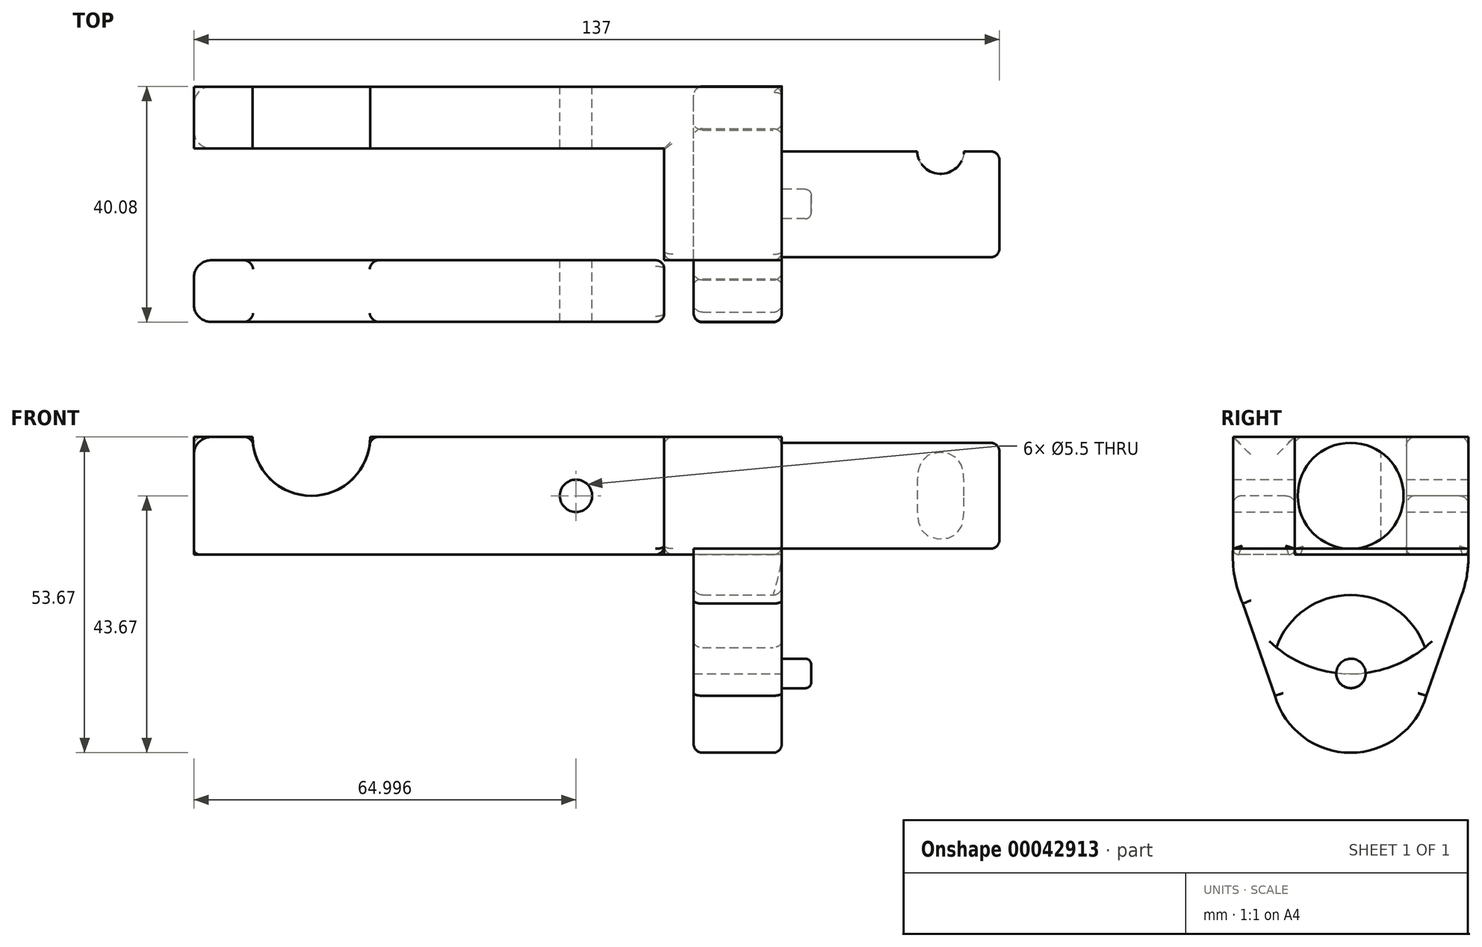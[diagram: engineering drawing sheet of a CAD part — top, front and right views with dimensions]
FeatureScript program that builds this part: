
annotation { "Feature Type Name" : "Feature", "Feature Type Description" : "" }
export const myFeature = defineFeature(function(context is Context, id is Id, definition is map)
    precondition{}
    {
        {
            var Q0;
            Q0=qCreatedBy(makeId("Top.planeOp"),FACE);
            var sketch = newSketch(context, id + "F0", { "sketchPlane" : qUnion([Q0])});
            skLineSegment(sketch, "E0.bottom", {"start": v(-43.64, 0) * mm, "end": v(37.87, 0) * mm});
            skLineSegment(sketch, "E0.top", {"start": v(-43.64, -10.5) * mm, "end": v(37.87, -10.5) * mm});
            skLineSegment(sketch, "E0.left", {"start": v(-43.64, 0) * mm, "end": v(-43.64, -10.5) * mm});
            skLineSegment(sketch, "E0.right", {"start": v(37.87, 0) * mm, "end": v(37.87, -10.5) * mm});
            skLineSegment(sketch, "E1.bottom", {"start": v(36.36, 0) * mm, "end": v(56.36, 0) * mm});
            skLineSegment(sketch, "E1.top", {"start": v(36.36, -40) * mm, "end": v(56.36, -40) * mm});
            skLineSegment(sketch, "E1.left", {"start": v(36.36, 0) * mm, "end": v(36.36, -40) * mm});
            skLineSegment(sketch, "E1.right", {"start": v(56.36, 0) * mm, "end": v(56.36, -40) * mm});
            skPoint(sketch, "E2.oppositeSnap0", {"position": v(46.36, -40) * mm});
            skLineSegment(sketch, "E2.bottom", {"start": v(56.36, -29.5) * mm, "end": v(-43.64, -29.5) * mm});
            skLineSegment(sketch, "E2.top", {"start": v(56.36, -40) * mm, "end": v(-43.64, -40) * mm});
            skLineSegment(sketch, "E2.left", {"start": v(56.36, -29.5) * mm, "end": v(56.36, -40) * mm});
            skLineSegment(sketch, "E2.right", {"start": v(-43.64, -29.5) * mm, "end": v(-43.64, -40) * mm});
            skSolve(sketch);
        }
        {
            var Q0;
            {var subQ3=sQuery(id+"F0.wireOp",EDGE,"E0.bottom");Q0=makeQuery(id+"F0.imprint","IMPRINT",FACE,{"disambiguationData":[TD([[makeQuery(id+"F0.imprint","IMPRINT",EDGE,{"derivedFrom":subQ3}),-1.0]])]});}
            var Q1;
            {var subQ6=sQuery(id+"F0.wireOp",EDGE,"E0.right");Q1=makeQuery(id+"F0.imprint","IMPRINT",FACE,{"disambiguationData":[TD([[makeQuery(id+"F0.imprint","IMPRINT",EDGE,{"derivedFrom":subQ6}),1.0]])]});}
            var Q2;
            {var subQ5=sQuery(id+"F0.wireOp",EDGE,"E0.right");Q2=makeQuery(id+"F0.imprint","IMPRINT",FACE,{"disambiguationData":[TD([[makeQuery(id+"F0.imprint","IMPRINT",EDGE,{"derivedFrom":subQ5}),-1.0]])]});}
            var Q3;
            {var subQ0=sQuery(id+"F0.wireOp",EDGE,"E2.right");Q3=makeQuery(id+"F0.imprint","IMPRINT",FACE,{"disambiguationData":[TD([[makeQuery(id+"F0.imprint","IMPRINT",EDGE,{"derivedFrom":subQ0}),1.0]])]});}
            var Q4;
            {var subQ0=sQuery(id+"F0.wireOp",EDGE,"E2.left");Q4=makeQuery(id+"F0.imprint","IMPRINT",FACE,{"disambiguationData":[TD([[makeQuery(id+"F0.imprint","IMPRINT",EDGE,{"derivedFrom":subQ0}),-1.0]])]});}
            extrude(context, id + "F1", {"entities" : qUnion([Q0, Q1, Q2, Q3, Q4]), "depth" : 20 * mm});
        }
        {
            var Q0;
            Q0=makeQuery(id+"F1.opExtrude","SWEPT_FACE",FACE,{"disambiguationData":[OSD([sQuery(id+"F0.wireOp",EDGE,"E2.top")])]});
            var sketch = newSketch(context, id + "F2", { "sketchPlane" : qUnion([Q0])});
            skArc(sketch, "E3", {"start": v(-33.64, 20) * mm, "mid": v(-23.64, 10) * mm, "end": v(-13.64, 20) * mm});
            skSolve(sketch);
        }
        {
            var Q0;
            {var subQ1=sQuery(id+"F2.wireOp",EDGE,"E3");Q0=makeQuery(id+"F2.imprint","IMPRINT",FACE,{"disambiguationData":[TD([[makeQuery(id+"F2.imprint","IMPRINT",EDGE,{"derivedFrom":subQ1}),1.0]])]});}
            extrude(context, id + "F3", {"entities" : qUnion([Q0]), "operationType" : NewBodyOperationType.REMOVE, "oppositeDirection" : true, "depth" : 52.24 * mm});
        }
        {
            var Q0;
            Q0=makeQuery(id+"F1.opExtrude","SWEPT_FACE",FACE,{"disambiguationData":[OSD([sQuery(id+"F0.wireOp",EDGE,"E0.bottom"),sQuery(id+"F0.wireOp",EDGE,"E1.bottom")])]});
            var sketch = newSketch(context, id + "F4", { "sketchPlane" : qUnion([Q0])});
            skCircle(sketch, "E4", {"center": v(-21.36, 10) * mm, "radius": 2.75 * mm});
            skSolve(sketch);
        }
        {
            var Q0;
            Q0=makeQuery(id+"F1.opExtrude","SWEPT_FACE",FACE,{"disambiguationData":[OSD([sQuery(id+"F0.wireOp",EDGE,"E1.right"),sQuery(id+"F0.wireOp",EDGE,"E2.left")])]});
            var sketch = newSketch(context, id + "F5", { "sketchPlane" : qUnion([Q0])});
            skCircle(sketch, "E5", {"center": v(-20, 10) * mm, "radius": 9 * mm});
            skPoint(sketch, "E5.centerSnap0", {"position": v(-20, 19) * mm});
            skPoint(sketch, "E5.centerSnap1", {"position": v(-40, 10) * mm});
            skSolve(sketch);
        }
        {
            var Q0;
            Q0=makeQuery(id+"F4.imprint","IMPRINT",FACE,{"disambiguationData":[TD([[makeQuery(id+"F4.imprint","IMPRINT",EDGE,{"derivedFrom":sQuery(id+"F4.wireOp",EDGE,"E4")}),1.0]])]});
            extrude(context, id + "F6", {"entities" : qUnion([Q0]), "operationType" : NewBodyOperationType.REMOVE, "oppositeDirection" : true, "depth" : 50.64 * mm});
        }
        {
            var Q0;
            {var subQ0=sQuery(id+"F0.wireOp",EDGE,"E1.right");var subQ1=sQuery(id+"F0.wireOp",EDGE,"E2.left");var subQ2=makeQuery(id+"F1.opExtrude","SWEPT_FACE",FACE,{"disambiguationData":[OSD([subQ0,subQ1])]});var subQ3=sQuery(id+"F0.wireOp",EDGE,"E0.bottom");var subQ4=sQuery(id+"F0.wireOp",EDGE,"E1.bottom");var subQ5=makeQuery(id+"F1.opExtrude","SWEPT_FACE",FACE,{"disambiguationData":[OSD([subQ3,subQ4])]});Q0=makeQuery(id+"FOvGjot31i7O7Zv_1.boolean.opBoolean","SPLIT",FACE,{"disambiguationData":[TD([subQ5])],"derivedFrom":subQ2});}
            var sketch = newSketch(context, id + "F7", { "sketchPlane" : qUnion([Q0])});
            skArc(sketch, "E6", {"start": v(-40, 1) * mm, "mid": v(-20, -20.26) * mm, "end": v(0, 1) * mm});
            skLineSegment(sketch, "E7", {"start": v(-40, 1) * mm, "end": v(0, 1) * mm});
            skCircle(sketch, "E8", {"center": v(-20, -20.26) * mm, "radius": 13.4 * mm});
            skLineSegment(sketch, "E9", {"start": v(-32.88, -23.99) * mm, "end": v(-39.4, -5.25) * mm});
            skLineSegment(sketch, "E10", {"start": v(-7.12, -23.99) * mm, "end": v(-0.52, -5.25) * mm});
            skSolve(sketch);
        }
        {
            var Q0;
            Q0 = qSketchRegion(id + "F7", true);
            var Q1;
            {var subQ0=sQuery(id+"F7.wireOp",EDGE,"E8");var subQ1=sQuery(id+"F7.wireOp",EDGE,"E6");var subQ3=makeQuery(id+"F7.imprint","INTERSECT",VERTEX,{"disambiguationData":[OD(0.0)],"derivedFrom":[subQ1,subQ0]});Q1=makeQuery(id+"F7.imprint","IMPRINT",FACE,{"disambiguationData":[TD([[makeQuery(id+"F7.imprint","IMPRINT",EDGE,{"disambiguationData":[TD([[subQ3,-1.0]])],"derivedFrom":subQ1}),1.0]])]});}
            extrude(context, id + "F8", {"entities" : qUnion([Q0, Q1]), "oppositeDirection" : true, "depth" : 15 * mm});
        }
        {
            var Q0;
            Q0=makeQuery(id+"F1.opExtrude","SWEPT_BODY",BODY,{"disambiguationData":[OSD([sQuery(id+"F0.wireOp",EDGE,"E0.bottom"),sQuery(id+"F0.wireOp",EDGE,"E0.top"),sQuery(id+"F0.wireOp",EDGE,"E0.left"),sQuery(id+"F0.wireOp",EDGE,"E1.bottom"),sQuery(id+"F0.wireOp",EDGE,"E1.left"),sQuery(id+"F0.wireOp",EDGE,"E1.right"),sQuery(id+"F0.wireOp",EDGE,"E2.bottom"),sQuery(id+"F0.wireOp",EDGE,"E2.top"),sQuery(id+"F0.wireOp",EDGE,"E2.left"),sQuery(id+"F0.wireOp",EDGE,"E2.right")])]});
            transform(context, id + "F9", {"entities" : qUnion([Q0]), "transformType" : TransformType.TRANSLATION_3D, "dx" : 0 * mm, "dy" : 0 * mm, "dz" : 0 * mm, "makeCopy" : true});
        }
        {
            var Q0;
            Q0 = qSketchRegion(id + "F5", true);
            extrude(context, id + "F10", {"entities" : qUnion([Q0]), "depth" : 37 * mm});
        }
        {
            var Q0;
            {var subQ0=sQuery(id+"F0.wireOp",EDGE,"E0.bottom");var subQ1=sQuery(id+"F0.wireOp",EDGE,"E0.top");var subQ2=sQuery(id+"F0.wireOp",EDGE,"E1.bottom");var subQ3=sQuery(id+"F0.wireOp",EDGE,"E1.left");var subQ4=sQuery(id+"F0.wireOp",EDGE,"E1.right");var subQ5=sQuery(id+"F0.wireOp",EDGE,"E2.bottom");var subQ6=sQuery(id+"F0.wireOp",EDGE,"E2.top");var subQ7=sQuery(id+"F0.wireOp",EDGE,"E2.left");Q0=makeQuery(id+"F3.boolean.opBoolean","SPLIT",FACE,{"disambiguationData":[TD([makeQuery(id+"F1.opExtrude","SWEPT_FACE",FACE,{"disambiguationData":[OSD([subQ3])]})])],"derivedFrom":makeQuery(id+"F1.opExtrude","CAP_FACE",FACE,{"disambiguationData":[OSD([subQ0,subQ1,sQuery(id+"F0.wireOp",EDGE,"E0.left"),subQ2,subQ3,subQ4,subQ5,subQ6,subQ7,sQuery(id+"F0.wireOp",EDGE,"E2.right")])],"isStart":false})});}
            var sketch = newSketch(context, id + "F11", { "sketchPlane" : qUnion([Q0])});
            skArc(sketch, "E11", {"start": v(79.36, -29.28) * mm, "mid": v(83.34, -25.17) * mm, "end": v(87.35, -29.25) * mm});
            skLineSegment(sketch, "E12", {"start": v(79.36, -29.28) * mm, "end": v(87.35, -29.25) * mm});
            skArc(sketch, "E13", {"start": v(79.36, -10.7) * mm, "mid": v(83.3, -14.8) * mm, "end": v(87.35, -10.8) * mm});
            skLineSegment(sketch, "E14", {"start": v(79.36, -10.7) * mm, "end": v(87.35, -10.8) * mm});
            skSolve(sketch);
        }
        {
            var Q0;
            Q0=makeQuery(id+"F11.imprint","IMPRINT",FACE,{"disambiguationData":[TD([[makeQuery(id+"F11.imprint","IMPRINT",EDGE,{"derivedFrom":sQuery(id+"F11.wireOp",EDGE,"bea93a81-216b-46dd-bc57-cd59c5f029c9")}),1.0]])]});
            var Q1;
            Q1=makeQuery(id+"F11.imprint","IMPRINT",FACE,{"disambiguationData":[TD([[makeQuery(id+"F11.imprint","IMPRINT",EDGE,{"derivedFrom":sQuery(id+"F11.wireOp",EDGE,"bffc142d-1d58-4124-9edf-efa4acdb14e5")}),1.0]])]});
            var Q2;
            Q2=makeQuery(id+"F11.imprint","IMPRINT",FACE,{"disambiguationData":[TD([[makeQuery(id+"F11.imprint","IMPRINT",EDGE,{"derivedFrom":sQuery(id+"F11.wireOp",EDGE,"E11")}),-1.0]])]});
            var Q3;
            Q3=makeQuery(id+"F11.imprint","IMPRINT",FACE,{"disambiguationData":[TD([[makeQuery(id+"F11.imprint","IMPRINT",EDGE,{"derivedFrom":sQuery(id+"F11.wireOp",EDGE,"E13")}),1.0]])]});
            extrude(context, id + "F12", {"entities" : qUnion([Q0, Q1, Q2, Q3]), "operationType" : NewBodyOperationType.REMOVE, "oppositeDirection" : true, "depth" : 25 * mm});
        }
        {
            var Q0;
            {var subQ0=sQuery(id+"F7.wireOp",EDGE,"E8");var subQ1=sQuery(id+"F7.wireOp",EDGE,"E6");var subQ5=makeQuery(id+"F7.imprint","INTERSECT",VERTEX,{"disambiguationData":[OD(0.0)],"derivedFrom":[subQ1,subQ0]});Q0=makeQuery(id+"F7.imprint","IMPRINT",FACE,{"disambiguationData":[TD([[makeQuery(id+"F7.imprint","IMPRINT",EDGE,{"disambiguationData":[TD([[subQ5,-1.0]])],"derivedFrom":subQ1}),-1.0]])]});}
            var sketch = newSketch(context, id + "F13", { "sketchPlane" : qUnion([Q0])});
            skCircle(sketch, "E15", {"center": v(-19.94, -20.2) * mm, "radius": 2.5 * mm});
            skSolve(sketch);
        }
        {
            var Q0;
            {var subQ0=sQuery(id+"F7.wireOp",EDGE,"E6");var subQ1=sQuery(id+"F7.wireOp",EDGE,"E8");var subQ2=makeQuery(id+"F7.imprint","IMPRINT",EDGE,{"disambiguationData":[TD([[makeQuery(id+"F7.imprint","INTERSECT",VERTEX,{"disambiguationData":[OD(0.0)],"derivedFrom":[subQ0,subQ1]}),-1.0]])],"derivedFrom":subQ0});var subQ3=sQuery(id+"F13.wireOp",EDGE,"E15");var subQ5=makeQuery(id+"F13.imprint","INTERSECT",VERTEX,{"disambiguationData":[OD(0.0)],"derivedFrom":[subQ2,subQ3]});Q0=makeQuery(id+"F13.imprint","IMPRINT",FACE,{"disambiguationData":[TD([[makeQuery(id+"F13.imprint","IMPRINT",EDGE,{"disambiguationData":[TD([[subQ5,-1.0]])],"derivedFrom":subQ3}),1.0]])]});}
            var Q1;
            {var subQ0=sQuery(id+"F7.wireOp",EDGE,"E6");var subQ1=sQuery(id+"F7.wireOp",EDGE,"E8");var subQ2=makeQuery(id+"F7.imprint","IMPRINT",EDGE,{"disambiguationData":[TD([[makeQuery(id+"F7.imprint","INTERSECT",VERTEX,{"disambiguationData":[OD(0.0)],"derivedFrom":[subQ0,subQ1]}),-1.0]])],"derivedFrom":subQ0});var subQ3=sQuery(id+"F13.wireOp",EDGE,"E15");var subQ5=makeQuery(id+"F13.imprint","INTERSECT",VERTEX,{"disambiguationData":[OD(0.0)],"derivedFrom":[subQ2,subQ3]});Q1=makeQuery(id+"F13.imprint","IMPRINT",FACE,{"disambiguationData":[TD([[makeQuery(id+"F13.imprint","IMPRINT",EDGE,{"disambiguationData":[TD([[subQ5,1.0]])],"derivedFrom":subQ3}),1.0]])]});}
            extrude(context, id + "F14", {"entities" : qUnion([Q0, Q1]), "operationType" : NewBodyOperationType.ADD, "depth" : 5 * mm});
        }
        {
            var Q0;
            {var subQ0=sQuery(id+"F0.wireOp",EDGE,"E0.bottom");var subQ1=sQuery(id+"F0.wireOp",EDGE,"E0.top");var subQ2=sQuery(id+"F0.wireOp",EDGE,"E1.bottom");var subQ3=sQuery(id+"F0.wireOp",EDGE,"E1.left");var subQ4=sQuery(id+"F0.wireOp",EDGE,"E1.right");var subQ5=sQuery(id+"F0.wireOp",EDGE,"E2.bottom");var subQ6=sQuery(id+"F0.wireOp",EDGE,"E2.top");var subQ7=sQuery(id+"F0.wireOp",EDGE,"E2.left");Q0=makeQuery(id+"F3.boolean.opBoolean","SPLIT",FACE,{"disambiguationData":[TD([makeQuery(id+"F1.opExtrude","SWEPT_FACE",FACE,{"disambiguationData":[OSD([subQ3])]})])],"derivedFrom":makeQuery(id+"F1.opExtrude","CAP_FACE",FACE,{"disambiguationData":[OSD([subQ0,subQ1,sQuery(id+"F0.wireOp",EDGE,"E0.left"),subQ2,subQ3,subQ4,subQ5,subQ6,subQ7,sQuery(id+"F0.wireOp",EDGE,"E2.right")])],"isStart":false})});}
            var Q1;
            {var subQ0=sQuery(id+"F0.wireOp",EDGE,"E0.bottom");var subQ1=sQuery(id+"F0.wireOp",EDGE,"E0.top");var subQ2=sQuery(id+"F0.wireOp",EDGE,"E0.left");var subQ3=sQuery(id+"F0.wireOp",EDGE,"E1.bottom");Q1=makeQuery(id+"F3.boolean.opBoolean","SPLIT",FACE,{"disambiguationData":[TD([makeQuery(id+"F1.opExtrude","SWEPT_FACE",FACE,{"disambiguationData":[OSD([subQ2])]})])],"derivedFrom":makeQuery(id+"F1.opExtrude","CAP_FACE",FACE,{"disambiguationData":[OSD([subQ0,subQ1,subQ2,subQ3,sQuery(id+"F0.wireOp",EDGE,"E1.left"),sQuery(id+"F0.wireOp",EDGE,"E1.right"),sQuery(id+"F0.wireOp",EDGE,"E2.bottom"),sQuery(id+"F0.wireOp",EDGE,"E2.top"),sQuery(id+"F0.wireOp",EDGE,"E2.left"),sQuery(id+"F0.wireOp",EDGE,"E2.right")])],"isStart":false})});}
            var Q2;
            {var subQ0=sQuery(id+"F0.wireOp",EDGE,"E2.bottom");var subQ1=sQuery(id+"F0.wireOp",EDGE,"E2.top");var subQ2=sQuery(id+"F0.wireOp",EDGE,"E2.right");Q2=makeQuery(id+"F3.boolean.opBoolean","SPLIT",FACE,{"disambiguationData":[TD([makeQuery(id+"F1.opExtrude","SWEPT_FACE",FACE,{"disambiguationData":[OSD([subQ2])]})])],"derivedFrom":makeQuery(id+"F1.opExtrude","CAP_FACE",FACE,{"disambiguationData":[OSD([sQuery(id+"F0.wireOp",EDGE,"E0.bottom"),sQuery(id+"F0.wireOp",EDGE,"E0.top"),sQuery(id+"F0.wireOp",EDGE,"E0.left"),sQuery(id+"F0.wireOp",EDGE,"E1.bottom"),sQuery(id+"F0.wireOp",EDGE,"E1.left"),sQuery(id+"F0.wireOp",EDGE,"E1.right"),subQ0,subQ1,sQuery(id+"F0.wireOp",EDGE,"E2.left"),subQ2])],"isStart":false})});}
            var Q3;
            Q3=makeQuery(id+"F3.boolean.opBoolean","COPY",FACE,{"disambiguationData":[OD(0.0)],"derivedFrom":makeQuery(id+"F3.opExtrude","SWEPT_FACE",FACE,{"disambiguationData":[OSD([sQuery(id+"F2.wireOp",EDGE,"E3")])]})});
            var Q4;
            Q4=makeQuery(id+"F3.boolean.opBoolean","COPY",FACE,{"disambiguationData":[OD(1.0)],"derivedFrom":makeQuery(id+"F3.opExtrude","SWEPT_FACE",FACE,{"disambiguationData":[OSD([sQuery(id+"F2.wireOp",EDGE,"E3")])]})});
            fillet(context, id + "F15", {"entities" : qUnion([Q0, Q1, Q2, Q3, Q4]), "radius" : 1.5 * mm, "tangentPropagation" : true, "allowEdgeOverflow" : false});
        }
        {
            var Q0;
            Q0=makeQuery(id+"F1.opExtrude","CAP_EDGE",EDGE,{"disambiguationData":[OSD([sQuery(id+"F0.wireOp",EDGE,"E2.right")])],"isStart":true});
            var Q1;
            Q1=makeQuery(id+"F1.opExtrude","CAP_EDGE",EDGE,{"disambiguationData":[OSD([sQuery(id+"F0.wireOp",EDGE,"E2.bottom")])],"isStart":true});
            var Q2;
            Q2=makeQuery(id+"F1.opExtrude","CAP_EDGE",EDGE,{"disambiguationData":[OSD([sQuery(id+"F0.wireOp",EDGE,"E2.top")])],"isStart":true});
            var Q3;
            Q3=makeQuery(id+"F1.opExtrude","CAP_EDGE",EDGE,{"disambiguationData":[OSD([sQuery(id+"F0.wireOp",EDGE,"E0.top")])],"isStart":true});
            var Q4;
            Q4=makeQuery(id+"F1.opExtrude","CAP_EDGE",EDGE,{"disambiguationData":[OSD([sQuery(id+"F0.wireOp",EDGE,"E0.left")])],"isStart":true});
            var Q5;
            Q5=makeQuery(id+"F1.opExtrude","CAP_EDGE",EDGE,{"disambiguationData":[OSD([sQuery(id+"F0.wireOp",EDGE,"E0.bottom"),sQuery(id+"F0.wireOp",EDGE,"E1.bottom")])],"isStart":true});
            fillet(context, id + "F16", {"entities" : qUnion([Q0, Q1, Q2, Q3, Q4, Q5]), "radius" : 1 * mm, "tangentPropagation" : true, "allowEdgeOverflow" : false});
        }
        {
            var Q0;
            {var subQ0=sQuery(id+"F7.wireOp",EDGE,"E6");var subQ1=sQuery(id+"F7.wireOp",EDGE,"E9");var subQ2=makeQuery(id+"F7.imprint","INTERSECT",VERTEX,{"disambiguationData":[OD(0.0)],"derivedFrom":[subQ0,subQ1]});Q0=makeQuery(id+"F8.opExtrude","CAP_EDGE",EDGE,{"disambiguationData":[OSD([subQ0]),TDD([makeQuery(id+"F7.imprint","IMPRINT",EDGE,{"disambiguationData":[TD([[subQ2,1.0]])],"derivedFrom":subQ0}),makeQuery(id+"F7.imprint","IMPRINT",EDGE,{"disambiguationData":[TD([[subQ2,-1.0]])],"derivedFrom":subQ0})])],"isStart":false});}
            var Q1;
            Q1=makeQuery(id+"F8.opExtrude","CAP_EDGE",EDGE,{"disambiguationData":[OSD([sQuery(id+"F7.wireOp",EDGE,"E10")])],"isStart":false});
            var Q2;
            Q2=makeQuery(id+"F8.opExtrude","CAP_EDGE",EDGE,{"disambiguationData":[OSD([sQuery(id+"F7.wireOp",EDGE,"E8")])],"isStart":false});
            fillet(context, id + "F17", {"entities" : qUnion([Q0, Q1, Q2]), "radius" : 1.5 * mm, "tangentPropagation" : true, "allowEdgeOverflow" : false});
        }
        {
            var Q0;
            Q0=makeQuery(id+"F8.opExtrude","CAP_EDGE",EDGE,{"disambiguationData":[OSD([sQuery(id+"F7.wireOp",EDGE,"E8")])],"isStart":true});
            var Q1;
            {var subQ0=sQuery(id+"F7.wireOp",EDGE,"E6");var subQ1=sQuery(id+"F7.wireOp",EDGE,"E9");var subQ2=makeQuery(id+"F7.imprint","INTERSECT",VERTEX,{"disambiguationData":[OD(0.0)],"derivedFrom":[subQ0,subQ1]});Q1=makeQuery(id+"F8.opExtrude","CAP_EDGE",EDGE,{"disambiguationData":[OSD([subQ0]),TDD([makeQuery(id+"F7.imprint","IMPRINT",EDGE,{"disambiguationData":[TD([[subQ2,1.0]])],"derivedFrom":subQ0}),makeQuery(id+"F7.imprint","IMPRINT",EDGE,{"disambiguationData":[TD([[subQ2,-1.0]])],"derivedFrom":subQ0})])],"isStart":true});}
            var Q2;
            Q2=makeQuery(id+"F1.opExtrude","SWEPT_EDGE",EDGE,{"disambiguationData":[OSD([sQuery(id+"F0.wireOp",EDGE,"E1.bottom"),sQuery(id+"F0.wireOp",EDGE,"E1.right")])]});
            var Q3;
            Q3=makeQuery(id+"F10.opExtrude","CAP_EDGE",EDGE,{"disambiguationData":[OSD([sQuery(id+"F5.wireOp",EDGE,"E5")])],"isStart":false});
            fillet(context, id + "F18", {"entities" : qUnion([Q0, Q1, Q2, Q3]), "radius" : 1.5 * mm, "tangentPropagation" : true, "allowEdgeOverflow" : false});
        }
        {
            var Q0;
            Q0=makeQuery(id+"F1.opExtrude","SWEPT_FACE",FACE,{"disambiguationData":[OSD([sQuery(id+"F0.wireOp",EDGE,"E0.left")])]});
            var Q1;
            Q1=makeQuery(id+"F1.opExtrude","SWEPT_FACE",FACE,{"disambiguationData":[OSD([sQuery(id+"F0.wireOp",EDGE,"E2.right")])]});
            fillet(context, id + "F19", {"entities" : qUnion([Q0, Q1]), "radius" : 3 * mm, "tangentPropagation" : true, "allowEdgeOverflow" : false});
        }
        {
            var Q0;
            Q0=makeQuery(id+"F1.opExtrude","CAP_EDGE",EDGE,{"disambiguationData":[OSD([sQuery(id+"F0.wireOp",EDGE,"E1.left")])],"isStart":true});
            fillet(context, id + "F20", {"entities" : qUnion([Q0]), "radius" : 1.5 * mm, "tangentPropagation" : true, "allowEdgeOverflow" : false});
        }
        {
            var Q0;
            Q0=makeQuery(id+"F14.opExtrude","CAP_EDGE",EDGE,{"disambiguationData":[OSD([sQuery(id+"F13.wireOp",EDGE,"E15")])],"isStart":false});
            fillet(context, id + "F21", {"entities" : qUnion([Q0]), "radius" : 1 * mm, "allowEdgeOverflow" : false});
        }
    });
